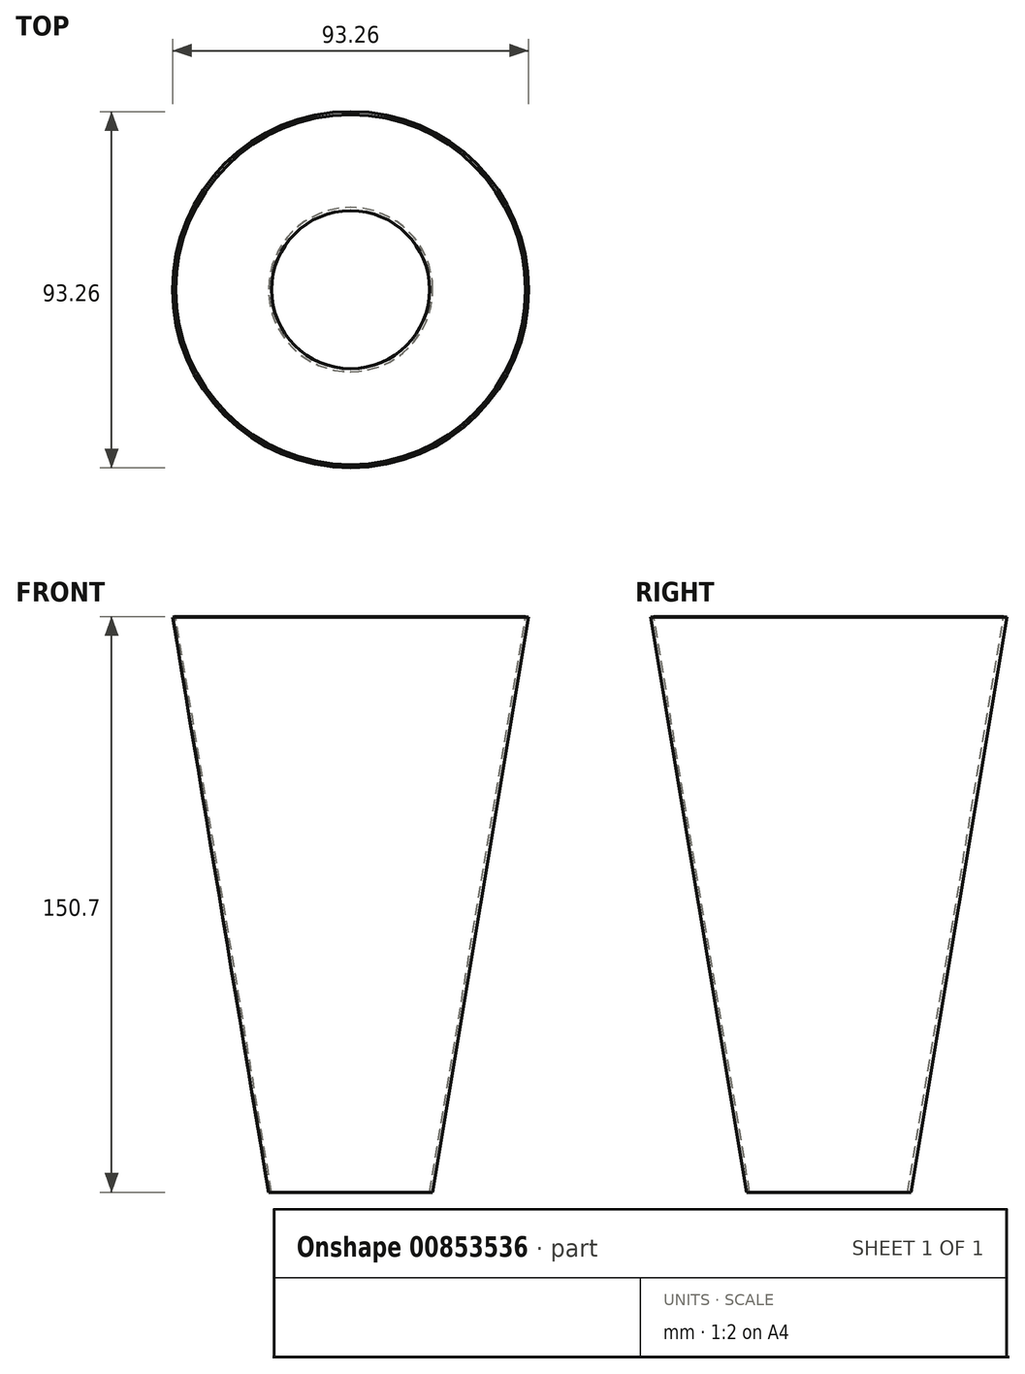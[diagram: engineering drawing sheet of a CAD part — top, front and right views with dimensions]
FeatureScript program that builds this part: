
annotation { "Feature Type Name" : "Feature", "Feature Type Description" : "" }
export const myFeature = defineFeature(function(context is Context, id is Id, definition is map)
    precondition{}
    {
        {
            var Q0;
            Q0=qCreatedBy(makeId("Front.planeOp"),FACE);
            var sketch = newSketch(context, id + "F0", { "sketchPlane" : qUnion([Q0])});
            skLineSegment(sketch, "E0", {"start": v(0, 0) * mm, "end": v(0, 65) * mm});
            skPoint(sketch, "E1.startSnap0", {"position": v(10.75, 0) * mm});
            skLineSegment(sketch, "E2", {"start": v(21.5, 0) * mm, "end": v(46.63, 150.57) * mm});
            skLineSegment(sketch, "E3", {"start": v(46.63, 150.57) * mm, "end": v(45.84, 150.7) * mm});
            skLineSegment(sketch, "E4", {"start": v(45.84, 150.7) * mm, "end": v(20.69, 0) * mm});
            skLineSegment(sketch, "E5", {"start": v(20.69, 0) * mm, "end": v(21.5, 0) * mm});
            skSolve(sketch);
        }
        {
            var Q0;
            Q0=makeQuery(id+"F0.imprint","IMPRINT",FACE,{"disambiguationData":[TD([[makeQuery(id+"F0.imprint","IMPRINT",EDGE,{"derivedFrom":sQuery(id+"F0.wireOp",EDGE,"E2")}),1.0]])]});
            var Q1;
            Q1=sQuery(id+"F0.wireOp",EDGE,"E0");
            revolve(context, id + "F1", {"surfaceOperationType" : NewSurfaceOperationType.NEW, "entities" : qUnion([Q0]), "axis" : qUnion([Q1]), "revolveType" : RevolveType.FULL});
        }
    });
